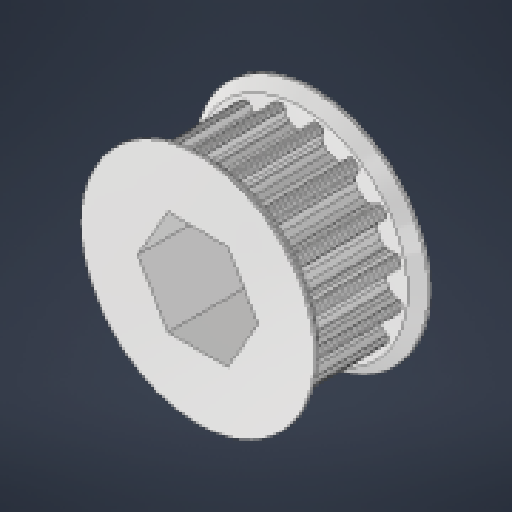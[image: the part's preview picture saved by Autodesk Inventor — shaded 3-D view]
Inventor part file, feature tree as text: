
AUTODESK INVENTOR PART (.ipt)
format: ipt  version: 2024.3 (Build 283343010, 343A)  size: 472,064 bytes
history: native  units: in
note: dims shown in document units (in); Inventor stores cm internally (conversion verified against a paired STEP export)
features: chamfer x1, other x1
ambient origin geometry x8: Origin, YZ Plane, XZ Plane, XY Plane, X Axis, Y Axis, Z Axis, Center Point
bodies: Solid1 (feature_tree)
feature tree (2):
  chamfer  "Chamfer1"  Distance=0.0492in Angle=45.0deg
  other  "Pulley"
